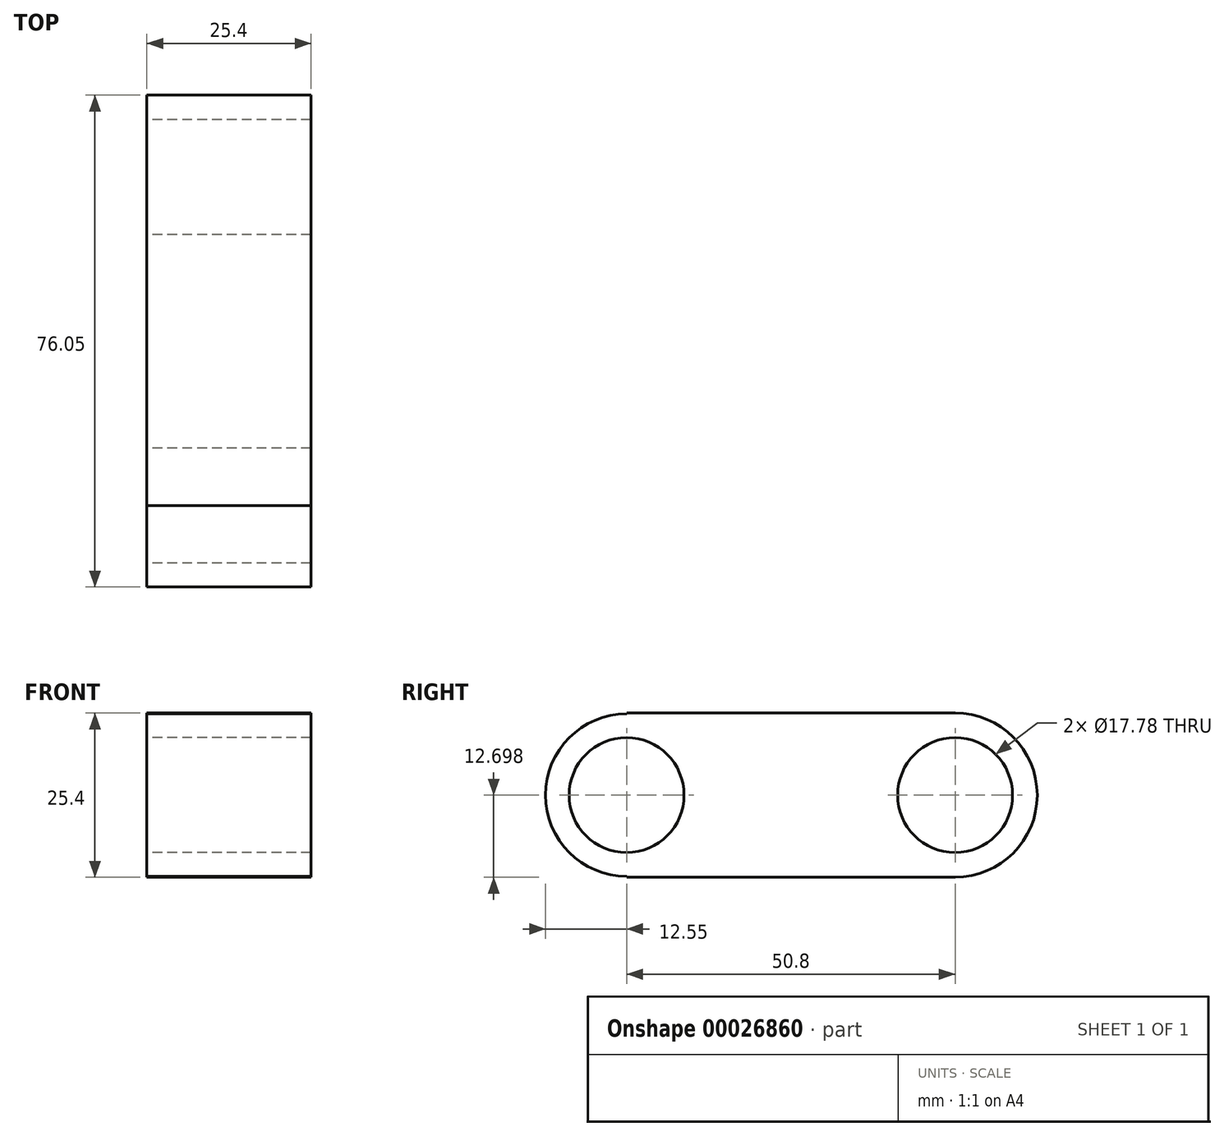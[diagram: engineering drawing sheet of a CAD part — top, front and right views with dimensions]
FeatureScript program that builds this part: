
annotation { "Feature Type Name" : "Feature", "Feature Type Description" : "" }
export const myFeature = defineFeature(function(context is Context, id is Id, definition is map)
    precondition{}
    {
        {
            var Q0;
            Q0=qCreatedBy(makeId("Right.planeOp"),FACE);
            var sketch = newSketch(context, id + "F0", { "sketchPlane" : qUnion([Q0])});
            skPoint(sketch, "E0.bottom.end.orphan", {"position": v(53.8, 14.5) * mm});
            skPoint(sketch, "E0.right.start.orphan", {"position": v(53.8, 6.74) * mm});
            skPoint(sketch, "E0.top.end.orphan", {"position": v(53.8, -1) * mm});
            skLineSegment(sketch, "E1.bottom", {"start": v(-11.41, 27.3) * mm, "end": v(39.39, 27.3) * mm});
            skLineSegment(sketch, "E1.top", {"start": v(-11.41, 1.9) * mm, "end": v(39.39, 1.9) * mm});
            skLineSegment(sketch, "E1.left", {"start": v(-11.41, 27.3) * mm, "end": v(-11.41, 27.16) * mm});
            skArc(sketch, "E2", {"start": v(39.39, 1.9) * mm, "mid": v(52.09, 14.6) * mm, "end": v(39.39, 27.3) * mm});
            skCircle(sketch, "E3", {"center": v(39.39, 14.6) * mm, "radius": 8.9 * mm});
            skArc(sketch, "E4", {"start": v(-11.41, 27.16) * mm, "mid": v(-23.96, 14.6) * mm, "end": v(-11.41, 2.06) * mm});
            skCircle(sketch, "E5", {"center": v(-11.41, 14.6) * mm, "radius": 8.9 * mm});
            skLineSegment(sketch, "E6.trimOffspring", {"start": v(-11.41, 2.06) * mm, "end": v(-11.41, 1.9) * mm});
            skSolve(sketch);
        }
        {
            var Q0;
            Q0=makeQuery(id+"F0.imprint","IMPRINT",FACE,{"disambiguationData":[TD([[makeQuery(id+"F0.imprint","IMPRINT",EDGE,{"derivedFrom":sQuery(id+"F0.wireOp",EDGE,"E1.bottom")}),-1.0]])]});
            extrude(context, id + "F1", {"entities" : qUnion([Q0]), "depth" : 25.4 * mm});
        }
    });
